# Revit family: JC KONTAKTER JCK227 Armbågskontakt
name_source: partatom
category: Specialty Equipment
units: mm (PartAtom-declared; Revit-internal decimal feet)

## family parameters
Always vertical = Yes
Cut with Voids When Loaded = No
Enable Cutting in Views = Yes
Host = Wall
Maintain Annotation Orientation = No
Part Type = Normal
Room Calculation Point = No
Round Connector Dimension = Use Diameter
Shared = No

## types (1)
- Armbågskontakt JCK227
    Antal microbrytare 2 = 1
    Antal mikrobrytare = 1
    CE Dokument = https://jckontakter.se
    Core Finish = Aluminum ENAW 6060
    Default Elevation = 0 mm  [stored 0 ft]
    Description = JCK227 tillhör en serie armbågskontakter med dubbla tryckytor som gör det möjligt att koppla t.ex. en extra dörr eller ett lås. JCK227 är tillverkad i silvereloxerad aluminium med svarta endcaps. Båda tryckytorna är utformade med fyra taktila rillor och fungerar som extra vägledning för personer med synnedsättning. Man kan enkelt känna sig till vart man ska trycka för att aktivera dörröppning.
    End Cap Finish = POM Tenac C 4520
    Lid Finish = Aluminum ENAW 6060
    Lägsta märkström = 1mA/4 V DC
    Manufacturer = JC Kontakter
    Mikrobrytare 1 = Standard NO IP67
    Mikrobrytare 2 = Standard NC IP67 (tre ledare)
    Model = JCK227
    Nominell märkström = 12 V - Resistive 6A Inductive L/R 5ms 6A, 24 V - Resistive 6A Inductive L/R 5ms 5A
    Placering av armbågskontakt = https://jckontakter.se
    Produktvikt = 0.383 kg
    Tekniskt produktblad = https://jckontakter.se
    Tillvalsförteckning = https://jckontakter.se
    Tillverkningsland = Sverige
    URL = https://jckontakter.se

note: [stored X ft] marks values corroborated as IEEE doubles in the binary element streams (Revit-internal decimal feet)

## geometry (parser evidence)
native form markers: Sweep x7
no freeform markers — native parametric forms only
